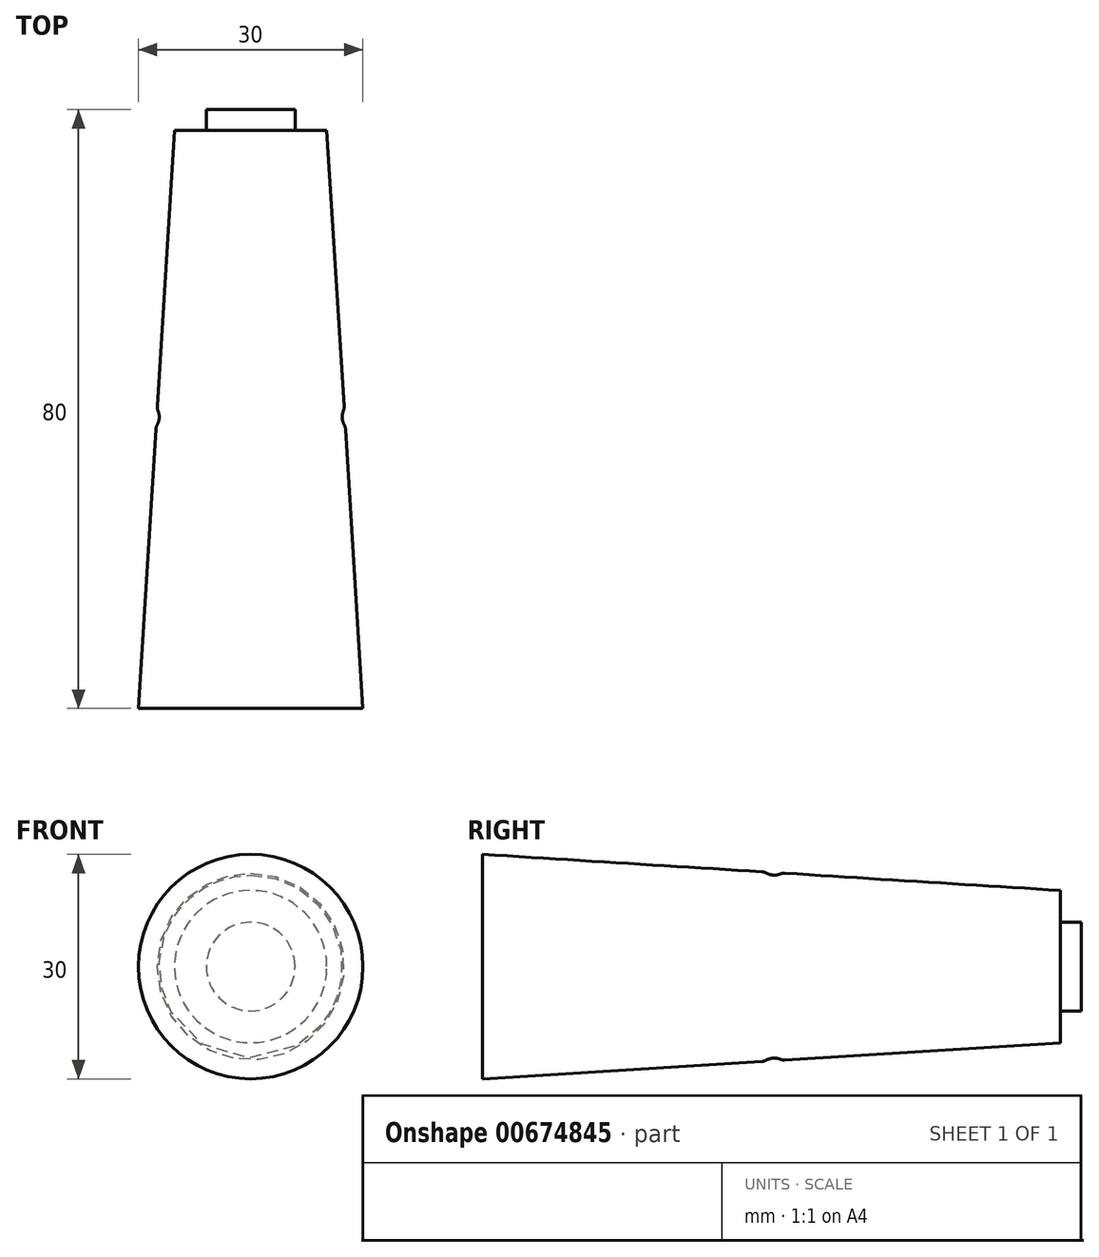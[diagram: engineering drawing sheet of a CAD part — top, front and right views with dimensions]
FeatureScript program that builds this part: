
annotation { "Feature Type Name" : "Feature", "Feature Type Description" : "" }
export const myFeature = defineFeature(function(context is Context, id is Id, definition is map)
    precondition{}
    {
        {
            var Q0;
            Q0=qCreatedBy(makeId("Top.planeOp"),FACE);
            var sketch = newSketch(context, id + "F0", { "sketchPlane" : qUnion([Q0])});
            skLineSegment(sketch, "E0.bottom", {"start": v(-7.5, 40) * mm, "end": v(2.5, 40) * mm});
            skLineSegment(sketch, "E0.top", {"start": v(-7.5, -40) * mm, "end": v(5.91, -40) * mm});
            skLineSegment(sketch, "E0.left", {"start": v(-7.5, 40) * mm, "end": v(-7.5, -40) * mm});
            skPoint(sketch, "E0.middle", {"position": v(0, 0) * mm});
            skLineSegment(sketch, "E1", {"start": v(-7.5, 40) * mm, "end": v(1.1, 40) * mm});
            skLineSegment(sketch, "E2", {"start": v(2.42, 41.2) * mm, "end": v(2.59, 38.6) * mm});
            skPoint(sketch, "E3.visualSharp", {"position": v(7.5, -40) * mm});
            skPoint(sketch, "E4.visualSharp", {"position": v(2.5, 40) * mm});
            skArc(sketch, "E4.filletArc", {"start": v(2.59, 38.6) * mm, "mid": v(2.12, 39.6) * mm, "end": v(1.1, 40) * mm});
            skArc(sketch, "E5", {"start": v(4.87, -0.26) * mm, "mid": v(4.73, -1.2) * mm, "end": v(4.99, -2.1) * mm});
            skLineSegment(sketch, "E6.trimOffspring", {"start": v(5.17, -2.72) * mm, "end": v(7.71, -43.4) * mm});
            skPoint(sketch, "E7.visualSharp", {"position": v(5, 0) * mm});
            skArc(sketch, "E7.filletArc", {"start": v(4.87, -0.26) * mm, "mid": v(4.96, 0.05) * mm, "end": v(4.98, 0.38) * mm});
            skPoint(sketch, "E8.visualSharp", {"position": v(5.15, -2.34) * mm});
            skArc(sketch, "E8.filletArc", {"start": v(5.17, -2.72) * mm, "mid": v(5.11, -2.4) * mm, "end": v(4.99, -2.1) * mm});
            skLineSegment(sketch, "E9", {"start": v(2.42, 41.2) * mm, "end": v(-1.58, 41.2) * mm});
            skLineSegment(sketch, "E10", {"start": v(-1.58, 41.2) * mm, "end": v(-1.58, 37.2) * mm});
            skLineSegment(sketch, "E11", {"start": v(-1.58, 37.2) * mm, "end": v(2.67, 37.2) * mm});
            skLineSegment(sketch, "E12.trimOffspring", {"start": v(2.67, 37.2) * mm, "end": v(4.98, 0.38) * mm});
            skLineSegment(sketch, "E13", {"start": v(-7.5, -40) * mm, "end": v(7.5, -40) * mm});
            skLineSegment(sketch, "E14", {"start": v(7.5, -40) * mm, "end": v(7.71, -43.4) * mm});
            skSolve(sketch);
        }
        {
            var Q0;
            {var subQ0=sQuery(id+"F0.wireOp",EDGE,"E0.left");Q0=makeQuery(id+"F0.imprint","IMPRINT",FACE,{"disambiguationData":[TD([[makeQuery(id+"F0.imprint","IMPRINT",EDGE,{"derivedFrom":subQ0}),1.0]])]});}
            var Q1;
            Q1=sQuery(id+"F0.wireOp",EDGE,"E0.left");
            revolve(context, id + "F1", {"entities" : qUnion([Q0]), "axis" : qUnion([Q1]), "revolveType" : RevolveType.FULL});
        }
    });
